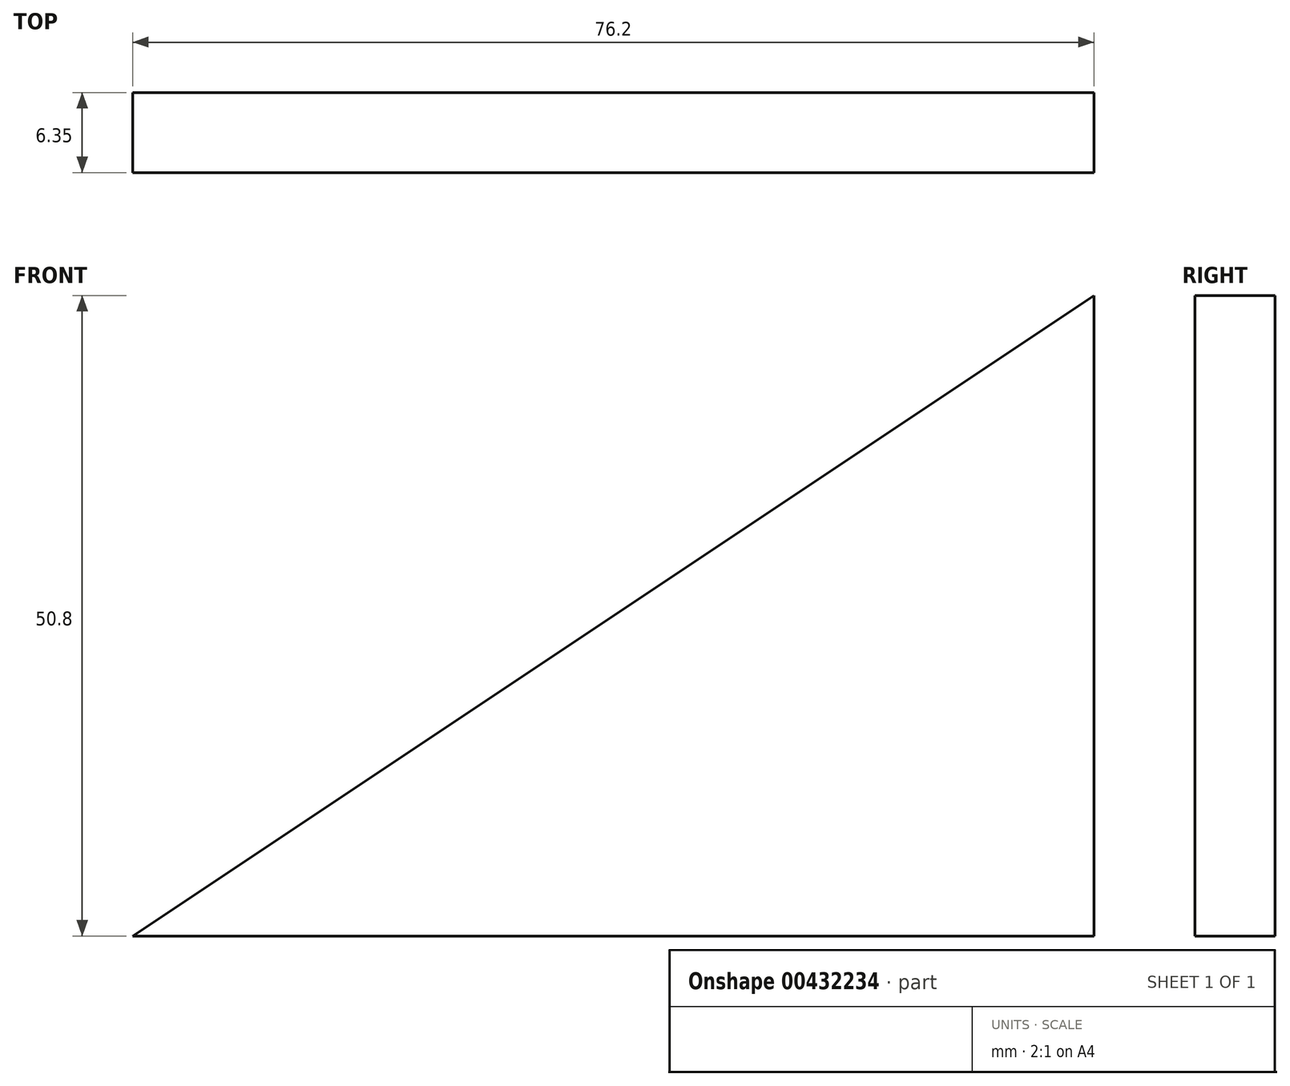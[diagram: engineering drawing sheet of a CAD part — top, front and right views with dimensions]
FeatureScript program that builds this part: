
annotation { "Feature Type Name" : "Feature", "Feature Type Description" : "" }
export const myFeature = defineFeature(function(context is Context, id is Id, definition is map)
    precondition{}
    {
        {
            var Q0;
            Q0=qCreatedBy(makeId("Front.planeOp"),FACE);
            var sketch = newSketch(context, id + "F0", { "sketchPlane" : qUnion([Q0])});
            skLineSegment(sketch, "E0", {"start": v(0, 0) * mm, "end": v(0, 50.8) * mm});
            skLineSegment(sketch, "E1", {"start": v(0, 0) * mm, "end": v(-76.2, 0) * mm});
            skLineSegment(sketch, "E2", {"start": v(-76.2, 0) * mm, "end": v(0, 50.8) * mm});
            skSolve(sketch);
        }
        {
            var Q0;
            Q0 = qSketchRegion(id + "F0", true);
            extrude(context, id + "F1", {"entities" : qUnion([Q0]), "depth" : 6.35 * mm});
        }
    });
